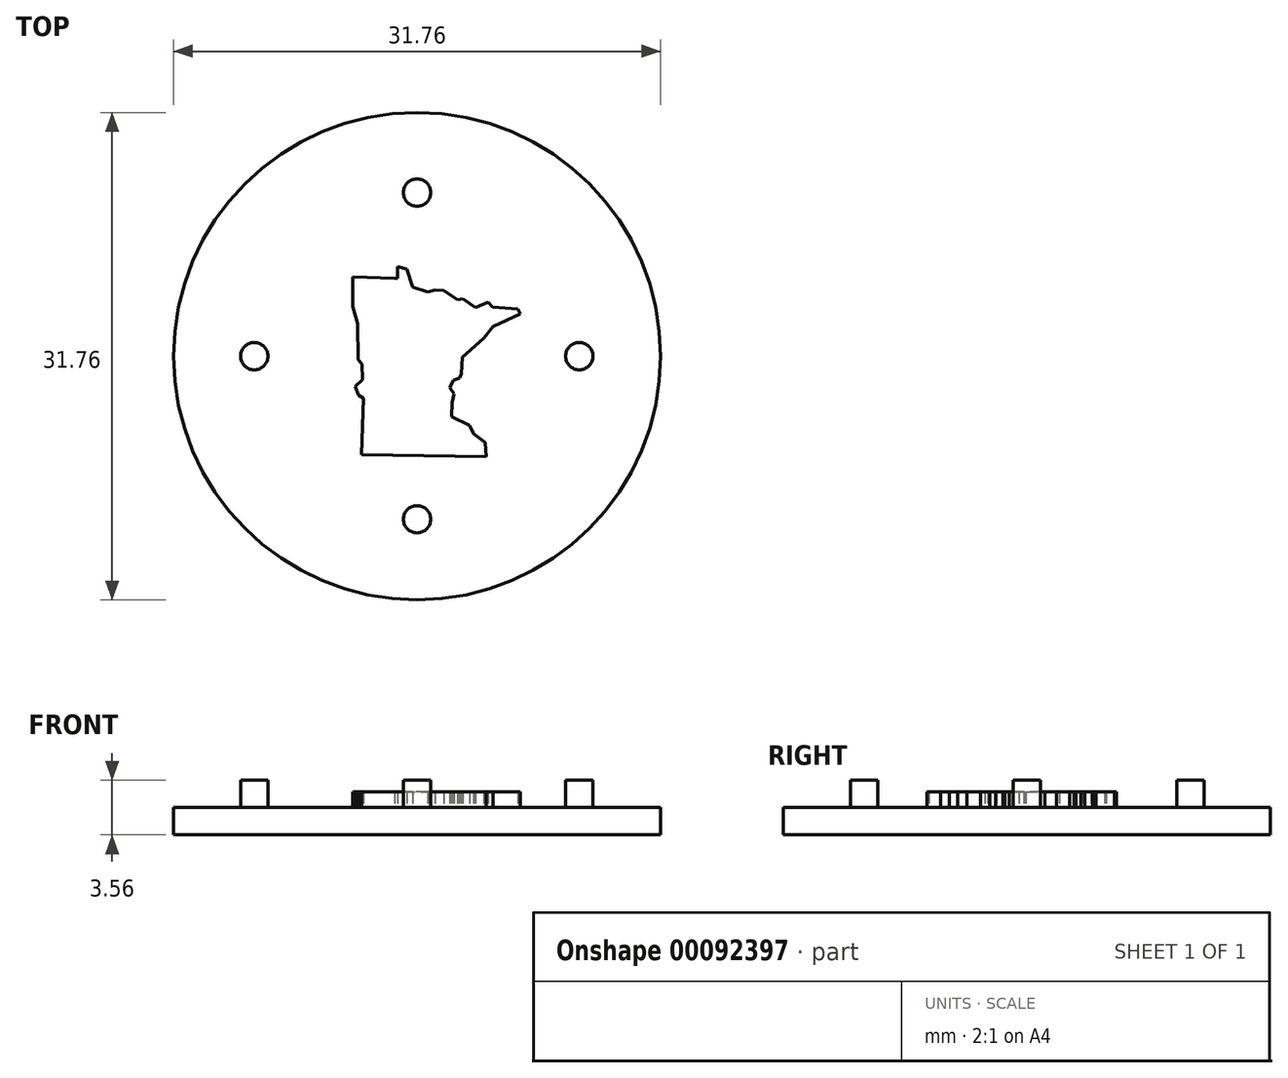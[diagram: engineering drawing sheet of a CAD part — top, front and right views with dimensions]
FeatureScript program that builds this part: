
annotation { "Feature Type Name" : "Feature", "Feature Type Description" : "" }
export const myFeature = defineFeature(function(context is Context, id is Id, definition is map)
    precondition{}
    {
        {
            var Q0;
            Q0=qCreatedBy(makeId("Top.planeOp"),FACE);
            var sketch = newSketch(context, id + "F0", { "sketchPlane" : qUnion([Q0])});
            skCircle(sketch, "E0", {"center": v(0, 0) * mm, "radius": 15.88 * mm});
            skSolve(sketch);
        }
        {
            var Q0;
            Q0=qSketchRegion(id+"F0",true);
            extrude(context, id + "F1", {"entities" : qUnion([Q0]), "oppositeDirection" : true, "depth" : 1.78 * mm});
        }
        {
            var Q0;
            Q0=makeQuery(id+"F1.opExtrude","CAP_FACE",FACE,{"disambiguationData":[OSD([sQuery(id+"F0.wireOp",EDGE,"E0")])],"isStart":true});
            var sketch = newSketch(context, id + "F2", { "sketchPlane" : qUnion([Q0])});
            skCircle(sketch, "E1", {"center": v(0, 0) * mm, "radius": 9.52 * mm});
            skSolve(sketch);
        }
        {
            var Q0;
            Q0=makeQuery(id+"F1.opExtrude","CAP_FACE",FACE,{"disambiguationData":[OSD([sQuery(id+"F0.wireOp",EDGE,"E0")])],"isStart":true});
            var sketch = newSketch(context, id + "F3", { "sketchPlane" : qUnion([Q0])});
            skCircle(sketch, "E2", {"center": v(0, 0) * mm, "radius": 7.62 * mm});
            skSolve(sketch);
        }
        {
            var Q0;
            Q0=makeQuery(id+"F3.imprint","IMPRINT",FACE,{"disambiguationData":[TD([[makeQuery(id+"F3.imprint","IMPRINT",EDGE,{"derivedFrom":sQuery(id+"F3.wireOp",EDGE,"E2")}),-1.0]])]});
            var sketch = newSketch(context, id + "F4", { "sketchPlane" : qUnion([Q0])});
            skCircle(sketch, "E3", {"center": v(0, 10.66) * mm, "radius": 0.89 * mm});
            skCircle(sketch, "E4", {"center": v(-10.61, 0) * mm, "radius": 0.89 * mm});
            skCircle(sketch, "E5", {"center": v(0, -10.63) * mm, "radius": 0.89 * mm});
            skCircle(sketch, "E6", {"center": v(10.57, 0) * mm, "radius": 0.89 * mm});
            skSolve(sketch);
        }
        {
            var Q0;
            Q0=qSketchRegion(id+"F4",true);
            extrude(context, id + "F5", {"entities" : qUnion([Q0]), "operationType" : NewBodyOperationType.ADD, "depth" : 1.78 * mm});
        }
        {
            var Q0;
            Q0=makeQuery(id+"F2.imprint","IMPRINT",FACE,{"disambiguationData":[TD([[makeQuery(id+"F2.imprint","IMPRINT",EDGE,{"derivedFrom":sQuery(id+"F2.wireOp",EDGE,"E1")}),-1.0]])]});
            var sketch = newSketch(context, id + "F6", { "sketchPlane" : qUnion([Q0])});
            skLineSegment(sketch, "E7", {"start": v(-1.45, 5.06) * mm, "end": v(-4.18, 5.16) * mm});
            skLineSegment(sketch, "E8", {"start": v(-4.18, 5.16) * mm, "end": v(-4.2, 3.23) * mm});
            skLineSegment(sketch, "E9", {"start": v(-4.2, 3.23) * mm, "end": v(-3.87, 2.12) * mm});
            skLineSegment(sketch, "E10", {"start": v(-3.87, 2.12) * mm, "end": v(-3.85, -0.21) * mm});
            skLineSegment(sketch, "E11", {"start": v(-3.85, -0.21) * mm, "end": v(-3.58, -0.53) * mm});
            skLineSegment(sketch, "E12", {"start": v(-3.58, -0.53) * mm, "end": v(-3.55, -1.51) * mm});
            skLineSegment(sketch, "E13", {"start": v(-3.55, -1.51) * mm, "end": v(-4.04, -1.98) * mm});
            skLineSegment(sketch, "E14", {"start": v(-4.04, -1.98) * mm, "end": v(-3.83, -2.54) * mm});
            skLineSegment(sketch, "E15", {"start": v(-3.83, -2.54) * mm, "end": v(-3.5, -2.73) * mm});
            skLineSegment(sketch, "E16", {"start": v(-3.5, -2.73) * mm, "end": v(-3.62, -6.4) * mm});
            skLineSegment(sketch, "E17", {"start": v(-3.62, -6.4) * mm, "end": v(4.5, -6.53) * mm});
            skLineSegment(sketch, "E18", {"start": v(4.5, -6.53) * mm, "end": v(4.45, -5.63) * mm});
            skLineSegment(sketch, "E19", {"start": v(4.45, -5.63) * mm, "end": v(3.7, -5.06) * mm});
            skLineSegment(sketch, "E20", {"start": v(3.7, -5.06) * mm, "end": v(3.42, -4.52) * mm});
            skLineSegment(sketch, "E21", {"start": v(3.42, -4.52) * mm, "end": v(2.26, -3.93) * mm});
            skLineSegment(sketch, "E22", {"start": v(2.26, -3.93) * mm, "end": v(2.28, -3.03) * mm});
            skLineSegment(sketch, "E23", {"start": v(2.28, -3.03) * mm, "end": v(2.4, -2.44) * mm});
            skLineSegment(sketch, "E24", {"start": v(2.4, -2.44) * mm, "end": v(2.14, -2.04) * mm});
            skLineSegment(sketch, "E25", {"start": v(2.14, -2.04) * mm, "end": v(2.37, -1.56) * mm});
            skLineSegment(sketch, "E26", {"start": v(2.37, -1.56) * mm, "end": v(2.77, -1.43) * mm});
            skLineSegment(sketch, "E27", {"start": v(2.77, -1.43) * mm, "end": v(2.87, -1.16) * mm});
            skLineSegment(sketch, "E28", {"start": v(2.87, -1.16) * mm, "end": v(2.96, -0.07) * mm});
            skLineSegment(sketch, "E29", {"start": v(2.96, -0.07) * mm, "end": v(4.34, 1.17) * mm});
            skLineSegment(sketch, "E30", {"start": v(4.34, 1.17) * mm, "end": v(4.95, 1.93) * mm});
            skLineSegment(sketch, "E31", {"start": v(4.95, 1.93) * mm, "end": v(6.71, 2.77) * mm});
            skLineSegment(sketch, "E32", {"start": v(6.71, 2.77) * mm, "end": v(6.57, 3.06) * mm});
            skLineSegment(sketch, "E33", {"start": v(6.57, 3.06) * mm, "end": v(4.93, 3.21) * mm});
            skLineSegment(sketch, "E34", {"start": v(4.93, 3.21) * mm, "end": v(4.64, 3.53) * mm});
            skLineSegment(sketch, "E35", {"start": v(4.64, 3.53) * mm, "end": v(3.82, 3.17) * mm});
            skLineSegment(sketch, "E36", {"start": v(3.82, 3.17) * mm, "end": v(2.98, 3.76) * mm});
            skLineSegment(sketch, "E37", {"start": v(2.98, 3.76) * mm, "end": v(2.62, 3.67) * mm});
            skLineSegment(sketch, "E38", {"start": v(2.62, 3.67) * mm, "end": v(1.74, 4.28) * mm});
            skLineSegment(sketch, "E39", {"start": v(1.74, 4.28) * mm, "end": v(1.17, 4.32) * mm});
            skLineSegment(sketch, "E40", {"start": v(1.17, 4.32) * mm, "end": v(0.69, 4.18) * mm});
            skLineSegment(sketch, "E41", {"start": v(0.69, 4.18) * mm, "end": v(-0.3, 4.51) * mm});
            skLineSegment(sketch, "E42", {"start": v(-0.3, 4.51) * mm, "end": v(-0.68, 5.69) * mm});
            skLineSegment(sketch, "E43", {"start": v(-0.68, 5.69) * mm, "end": v(-1.29, 5.84) * mm});
            skLineSegment(sketch, "E44", {"start": v(-1.29, 5.84) * mm, "end": v(-1.29, 5.06) * mm});
            skLineSegment(sketch, "E45", {"start": v(-1.29, 5.06) * mm, "end": v(-1.45, 5.06) * mm});
            skSolve(sketch);
        }
        {
            var Q0;
            Q0 = qSketchRegion(id + "F6", true);
            extrude(context, id + "F7", {"entities" : qUnion([Q0]), "operationType" : NewBodyOperationType.ADD, "depth" : 1.02 * mm});
        }
    });
